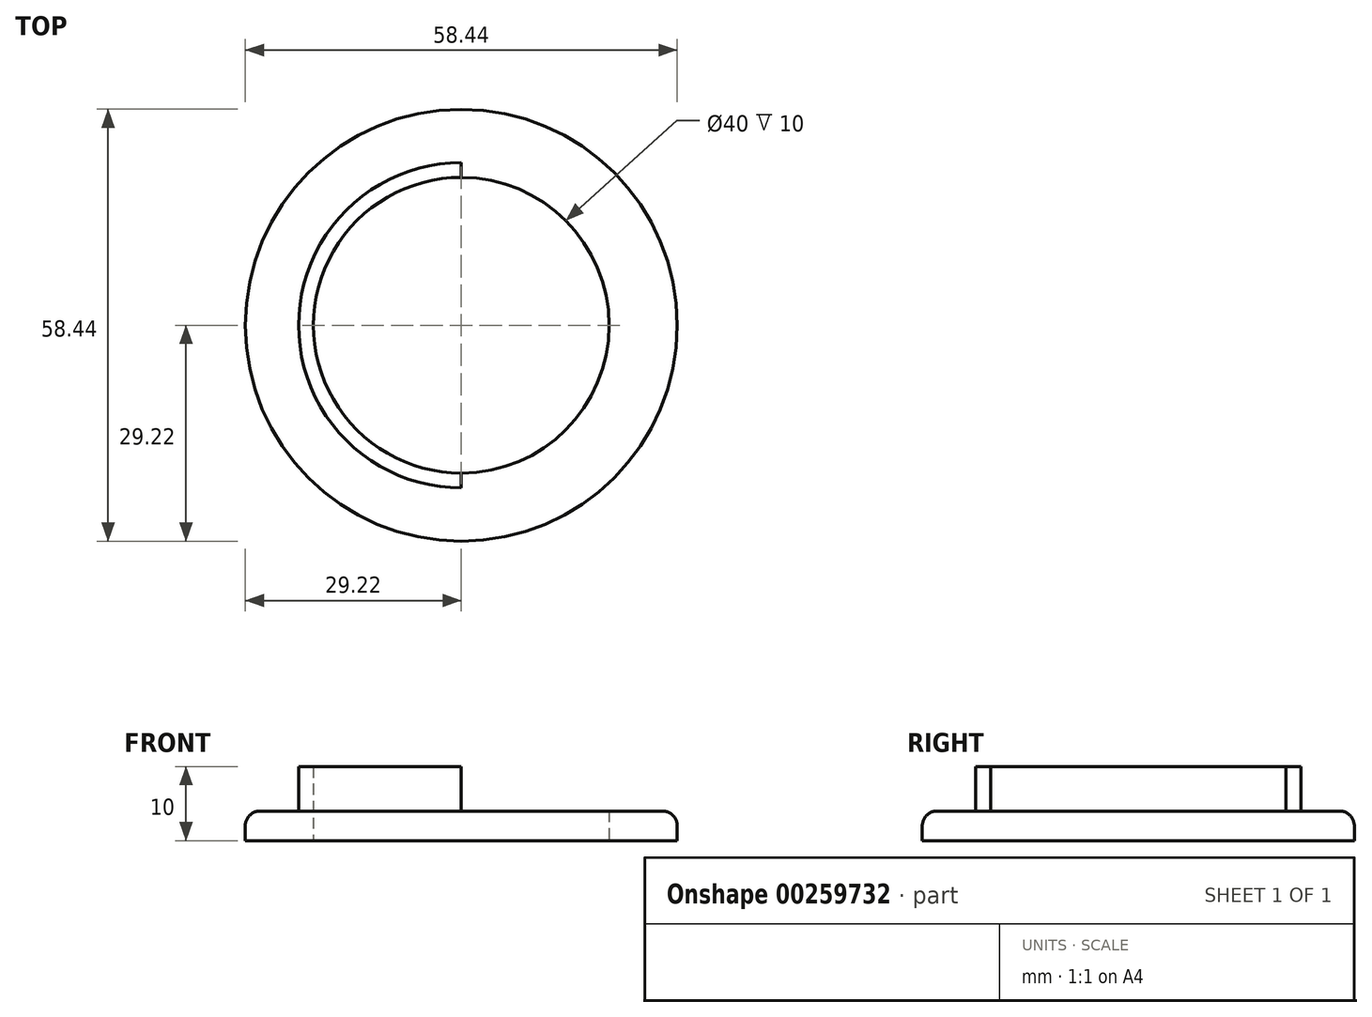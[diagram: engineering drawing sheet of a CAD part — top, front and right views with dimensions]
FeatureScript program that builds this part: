
annotation { "Feature Type Name" : "Feature", "Feature Type Description" : "" }
export const myFeature = defineFeature(function(context is Context, id is Id, definition is map)
    precondition{}
    {
        {
            var Q0;
            Q0=qCreatedBy(makeId("Top.planeOp"),FACE);
            var sketch = newSketch(context, id + "F0", { "sketchPlane" : qUnion([Q0])});
            skCircle(sketch, "E0", {"center": v(0, 0) * mm, "radius": 29.22 * mm});
            skCircle(sketch, "E1", {"center": v(0, 0) * mm, "radius": 20 * mm});
            skCircle(sketch, "E2.0", {"center": v(0, 0) * mm, "radius": 22 * mm});
            skLineSegment(sketch, "E3", {"start": v(0, -20) * mm, "end": v(0.01, -22) * mm});
            skLineSegment(sketch, "E4", {"start": v(0, 20) * mm, "end": v(0, 22) * mm});
            skSolve(sketch);
        }
        {
            var Q0;
            {var subQ0=sQuery(id+"F0.wireOp",EDGE,"E3");Q0=makeQuery(id+"F0.imprint","IMPRINT",FACE,{"disambiguationData":[TD([[makeQuery(id+"F0.imprint","IMPRINT",EDGE,{"derivedFrom":subQ0}),-1.0]])]});}
            extrude(context, id + "F1", {"entities" : qUnion([Q0]), "depth" : 10 * mm});
        }
        {
            var Q0;
            Q0=makeQuery(id+"F0.imprint","IMPRINT",FACE,{"disambiguationData":[TD([[makeQuery(id+"F0.imprint","IMPRINT",EDGE,{"derivedFrom":sQuery(id+"F0.wireOp",EDGE,"E0")}),1.0]])]});
            extrude(context, id + "F2", {"entities" : qUnion([Q0]), "operationType" : NewBodyOperationType.ADD, "depth" : 4 * mm});
        }
        {
            var Q0;
            Q0=makeQuery(id+"F2.opExtrude","CAP_EDGE",EDGE,{"disambiguationData":[OSD([sQuery(id+"F0.wireOp",EDGE,"E0")])],"isStart":false});
            fillet(context, id + "F3", {"entities" : qUnion([Q0]), "radius" : 2 * mm, "tangentPropagation" : true, "allowEdgeOverflow" : false});
        }
        {
            var Q0;
            {var subQ0=sQuery(id+"F0.wireOp",EDGE,"E3");Q0=makeQuery(id+"F0.imprint","IMPRINT",FACE,{"disambiguationData":[TD([[makeQuery(id+"F0.imprint","IMPRINT",EDGE,{"derivedFrom":subQ0}),1.0]])]});}
            extrude(context, id + "F4", {"entities" : qUnion([Q0]), "operationType" : NewBodyOperationType.ADD, "depth" : 4 * mm});
        }
    });
